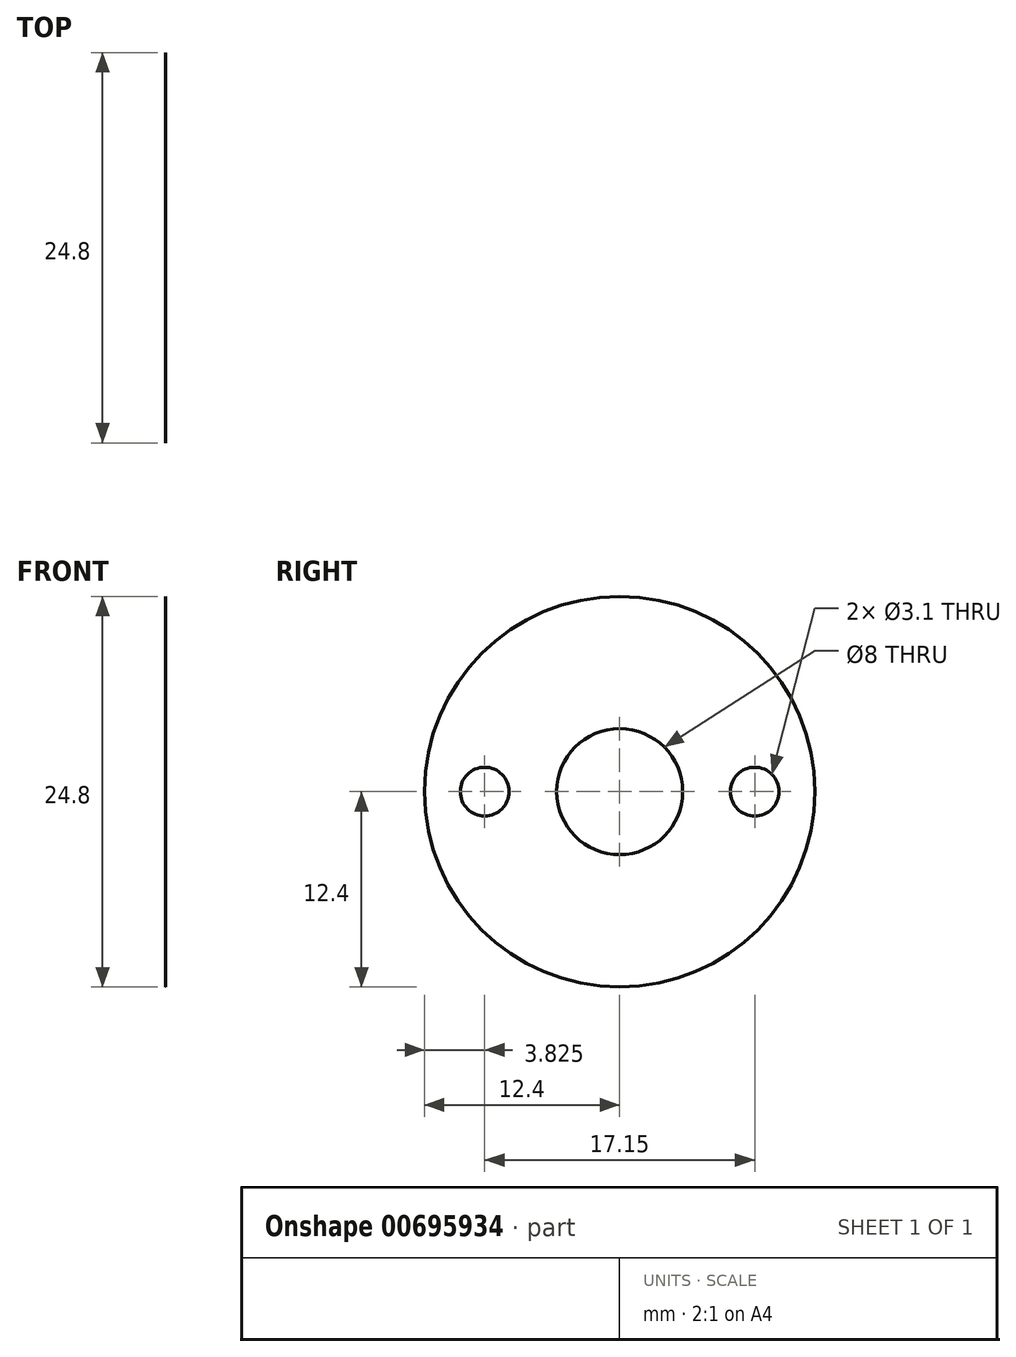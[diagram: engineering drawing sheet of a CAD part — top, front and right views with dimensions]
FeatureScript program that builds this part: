
annotation { "Feature Type Name" : "Feature", "Feature Type Description" : "" }
export const myFeature = defineFeature(function(context is Context, id is Id, definition is map)
    precondition{}
    {
        {
            var Q0;
            Q0=qCreatedBy(makeId("Right.planeOp"),FACE);
            var sketch = newSketch(context, id + "F0", { "sketchPlane" : qUnion([Q0])});
            skCircle(sketch, "E0", {"center": v(0, 0) * mm, "radius": 12.4 * mm});
            skCircle(sketch, "E1", {"center": v(0, 0) * mm, "radius": 4 * mm});
            skCircle(sketch, "E2", {"center": v(-8.57, 0) * mm, "radius": 1.55 * mm});
            skCircle(sketch, "E3", {"center": v(8.57, 0) * mm, "radius": 1.55 * mm});
            skLineSegment(sketch, "E4", {"start": v(-8.57, 0) * mm, "end": v(8.57, 0) * mm, "construction": true});
            skSolve(sketch);
        }
        {
            var Q0;
            Q0 = qSketchRegion(id + "F0", true);
            extrude(context, id + "F1", {"entities" : qUnion([Q0]), "depth" : 1 / 203.2 * mm, "offsetDistance" : 25 * mm});
        }
    });
